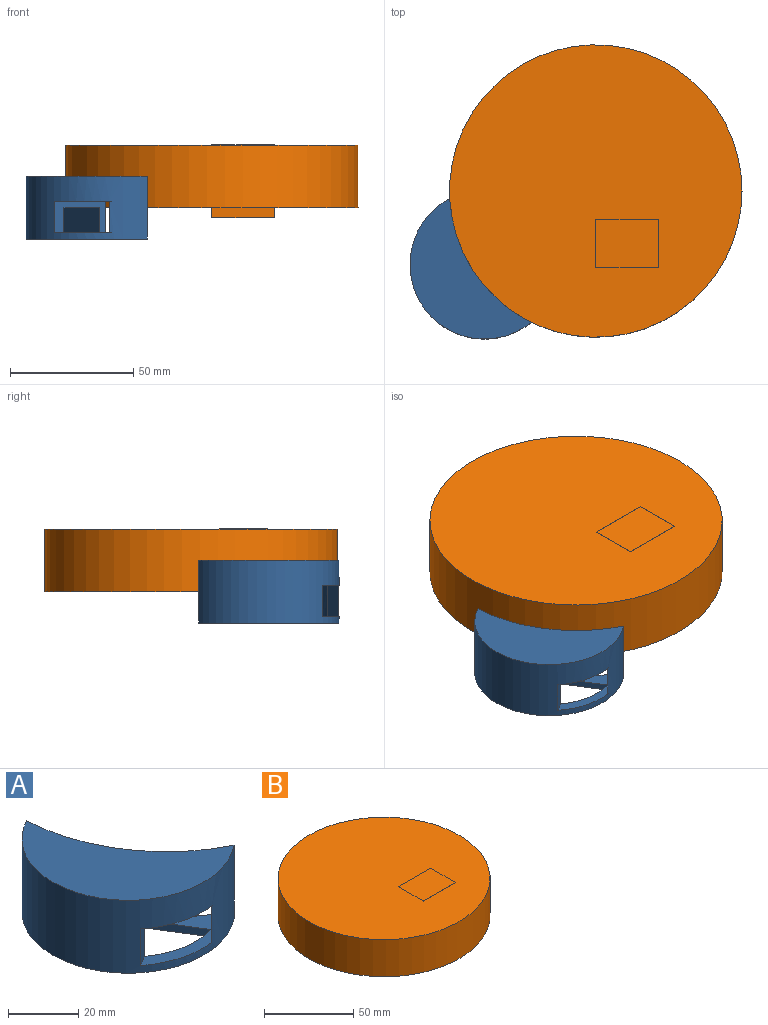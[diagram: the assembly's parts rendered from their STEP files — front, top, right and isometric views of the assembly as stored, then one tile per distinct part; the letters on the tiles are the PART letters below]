
ASSEMBLY  parts=2 mates=1
PART A: 17 faces, bbox 49.3x57x25.4 mm
  f0: cylinder r=30.25mm len=57.01mm, axis (0,0,1), area 2262.2mm2, adj f3,f4,f5,f9,f14,f15,f16
  f1: plane 42.19x26.22mm, normal (-0.85,-0.53,0), area 473.6mm2, adj f2,f4,f6,f9,f15
  f2: cylinder r=25.75mm len=43.26mm, axis (0,0,-1), area 609mm2, adj f1,f4,f6,f9,f15
  f3: cylinder r=59.35mm len=50.26mm, axis (0,0,1), area 734.1mm2, adj f0,f4,f5,f7,f8,f9,f10,f11
  f4: plane 57.01x49.31mm, normal (0,0,-1), area 586.8mm2, adj f0,f1,f2,f3
  f5: plane 57.01x49.31mm, normal (0,0,1), area 1282.7mm2, adj f0,f3
  f6: plane 38.12x24.92mm, normal (0,0,-1), area 520mm2, adj f1,f2,f15
  f7: plane 43.14x29.62mm, normal (0,0,1), area 702mm2, adj f3,f8,f10,f13,f15
  f8: plane 12.7x11.79mm, normal (0.85,0.53,0), area 176.3mm2, adj f3,f7,f11,f13
  f9: plane 35.34x19.39mm, normal (0,0,1), area 191.3mm2, adj f0,f1,f2,f3,f10,f14,f15
  f10: cylinder r=27.71mm len=51.69mm, axis (0,0,1), area 1158.5mm2, adj f3,f7,f9,f11,f12,f13,f14,f16
  f11: plane 25.6x17.28mm, normal (0,0,1), area 36mm2, adj f3,f8,f10,f13
  f12: plane 51.69x44.29mm, normal (0,0,-1), area 1039.8mm2, adj f3,f10
  f13: cylinder r=28.29mm len=22.46mm, axis (0,0,-1), area 322.5mm2, adj f7,f8,f10,f11
  f14: plane 12.7x7.4mm, normal (-0.53,0.85,0), area 110.7mm2, adj f0,f9,f10,f16
  f15: plane 20.7x12.87mm, normal (0.53,-0.85,0), area 134.8mm2, adj f0,f1,f2,f3,f6,f7,f9,f16
  f16: plane 29.76x7.95mm, normal (0,0,-1), area 65.3mm2, adj f0,f10,f14,f15
PART B: 15 faces, bbox 118.7x118.7x29.5 mm
  f0: cylinder r=59.35mm len=118.7mm, axis (0,0,-1), area 9471.5mm2, adj f1,f2
  f1: plane 118.7x118.7mm, normal (0,0,1), area 10567.8mm2, adj f0,f10,f11,f12,f13
  f2: plane 118.7x118.7mm, normal (0,0,-1), area 2365.2mm2, adj f0,f3
  f3: cylinder r=52.62mm len=105.25mm, axis (0,0,-1), area 4199.3mm2, adj f2,f4
  f4: plane 105.25x105.25mm, normal (0,0,-1), area 8202.6mm2, adj f3,f6,f7,f8,f9
  f5: plane 25.4x19.59mm, normal (0,0,-1), area 497.5mm2, adj f6,f7,f8,f9
  f6: plane 19.59x16.77mm, normal (-1,0,0), area 328.5mm2, adj f4,f5,f8,f9
  f7: plane 19.59x16.77mm, normal (1,0,0), area 328.5mm2, adj f4,f5,f8,f9
  f8: plane 25.4x16.77mm, normal (0,-1,0), area 425.9mm2, adj f4,f5,f6,f7
  f9: plane 25.4x16.77mm, normal (0,1,0), area 425.9mm2, adj f4,f5,f6,f7
  f10: plane 25.4x0.06mm, normal (0,1,0), area 1.6mm2, adj f1,f12,f13,f14
  f11: plane 25.4x0.06mm, normal (0,-1,0), area 1.6mm2, adj f1,f12,f13,f14
  f12: plane 19.59x0.06mm, normal (1,0,0), area 1.3mm2, adj f1,f10,f11,f14
  f13: plane 19.59x0.06mm, normal (-1,0,0), area 1.3mm2, adj f1,f10,f11,f14
  f14: plane 25.4x19.59mm, normal (0,0,1), area 497.5mm2, adj f10,f11,f12,f13
PLACE A t=(15.18,11.79,-8.92)mm
PLACE B t=(15.18,11.79,-21.62)mm
MATE fastened A.f3 <-> B.f0  axis (0,0,1) through (15.18,11.79,-21.62)mm
